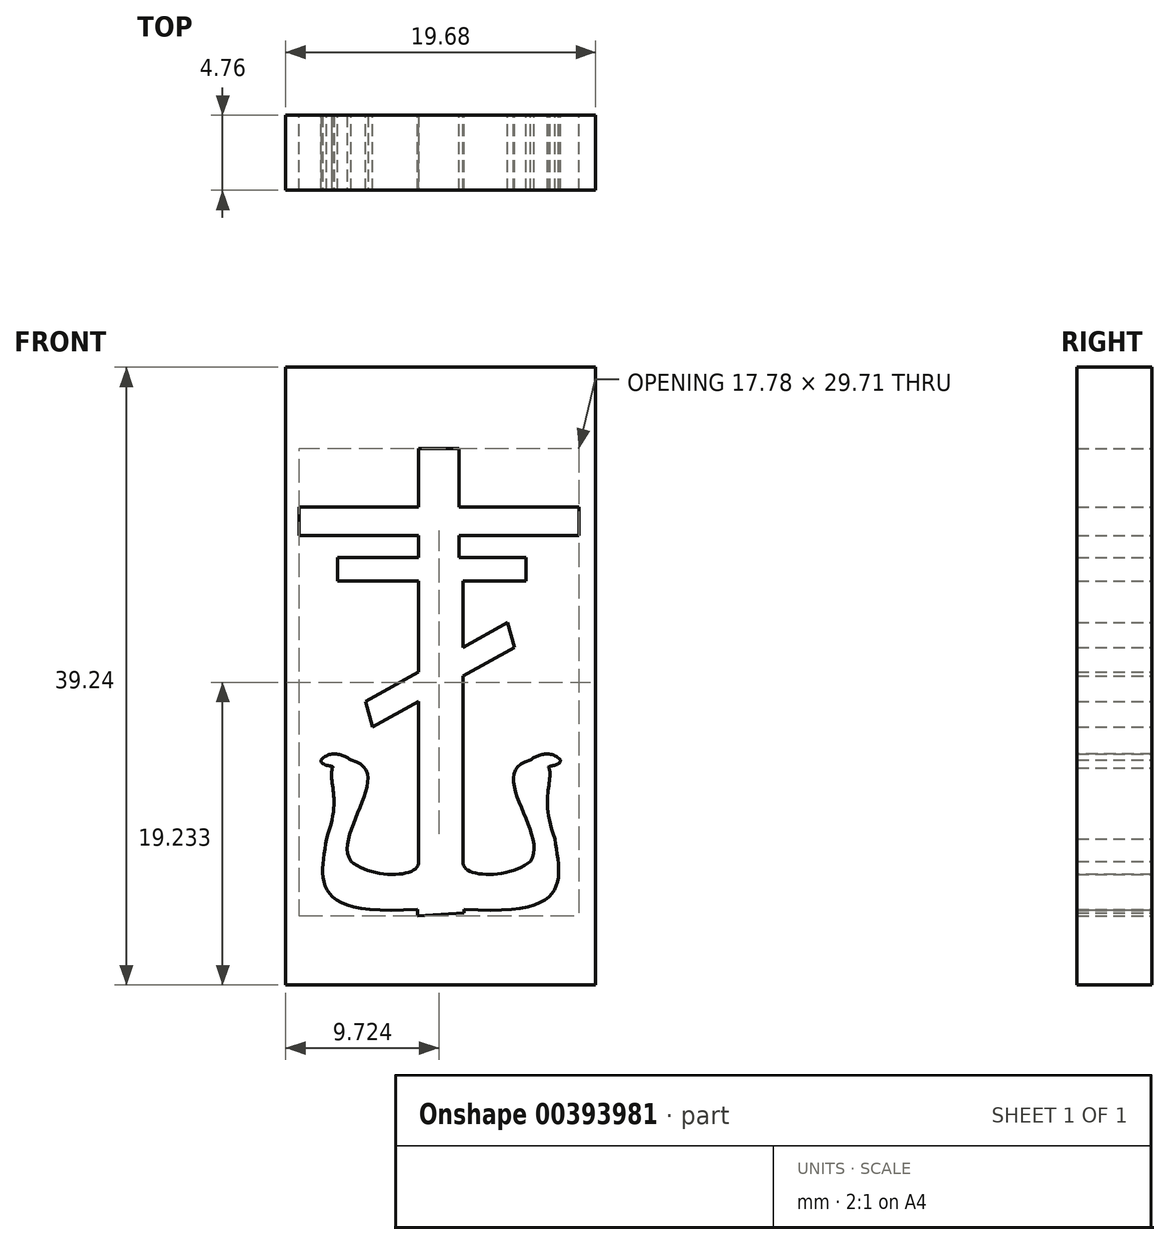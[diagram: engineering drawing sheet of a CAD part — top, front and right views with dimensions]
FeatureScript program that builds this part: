
annotation { "Feature Type Name" : "Feature", "Feature Type Description" : "" }
export const myFeature = defineFeature(function(context is Context, id is Id, definition is map)
    precondition{}
    {
        {
            var Q0;
            Q0=qCreatedBy(makeId("Front.planeOp"),FACE);
            var sketch = newSketch(context, id + "F0", { "sketchPlane" : qUnion([Q0])});
            skLineSegment(sketch, "E0", {"start": v(-1.42, 14.47) * mm, "end": v(1.15, 14.47) * mm});
            skLineSegment(sketch, "E1", {"start": v(1.15, 14.47) * mm, "end": v(1.15, 10.74) * mm});
            skLineSegment(sketch, "E2", {"start": v(1.15, 10.74) * mm, "end": v(8.77, 10.74) * mm});
            skLineSegment(sketch, "E3", {"start": v(8.77, 10.74) * mm, "end": v(8.77, 8.92) * mm});
            skLineSegment(sketch, "E4", {"start": v(8.77, 8.92) * mm, "end": v(1.15, 8.92) * mm});
            skLineSegment(sketch, "E5", {"start": v(1.15, 8.92) * mm, "end": v(1.15, 7.52) * mm});
            skLineSegment(sketch, "E6", {"start": v(1.15, 7.52) * mm, "end": v(5.42, 7.52) * mm});
            skLineSegment(sketch, "E7", {"start": v(5.42, 7.52) * mm, "end": v(5.42, 6.06) * mm});
            skLineSegment(sketch, "E8", {"start": v(5.42, 6.06) * mm, "end": v(1.42, 6.06) * mm});
            skLineSegment(sketch, "E9", {"start": v(1.42, 6.06) * mm, "end": v(1.42, 1.84) * mm});
            skLineSegment(sketch, "E10", {"start": v(1.42, 1.84) * mm, "end": v(4.24, 3.4) * mm});
            skLineSegment(sketch, "E11", {"start": v(4.68, 1.84) * mm, "end": v(4.24, 3.4) * mm});
            skLineSegment(sketch, "E12", {"start": v(4.68, 1.84) * mm, "end": v(1.42, 0) * mm});
            skLineSegment(sketch, "E13", {"start": v(1.42, 0) * mm, "end": v(1.42, -11.76) * mm});
            skLineSegment(sketch, "E14", {"start": v(-1.42, 14.47) * mm, "end": v(-1.42, 10.74) * mm});
            skLineSegment(sketch, "E15", {"start": v(-1.42, 10.74) * mm, "end": v(-9, 10.74) * mm});
            skLineSegment(sketch, "E16", {"start": v(-9, 10.74) * mm, "end": v(-9, 8.92) * mm});
            skLineSegment(sketch, "E17", {"start": v(-9, 8.92) * mm, "end": v(-1.42, 8.92) * mm});
            skLineSegment(sketch, "E18", {"start": v(-1.42, 8.92) * mm, "end": v(-1.42, 7.52) * mm});
            skLineSegment(sketch, "E19", {"start": v(-1.42, 7.52) * mm, "end": v(-6.54, 7.52) * mm});
            skLineSegment(sketch, "E20", {"start": v(-6.54, 7.52) * mm, "end": v(-6.54, 6.06) * mm});
            skLineSegment(sketch, "E21", {"start": v(-6.54, 6.06) * mm, "end": v(-1.42, 6.06) * mm});
            skLineSegment(sketch, "E22", {"start": v(-1.42, 6.06) * mm, "end": v(-1.42, 0.27) * mm});
            skLineSegment(sketch, "E23", {"start": v(-1.42, 0.27) * mm, "end": v(-4.78, -1.6) * mm});
            skLineSegment(sketch, "E24", {"start": v(-4.78, -1.6) * mm, "end": v(-4.31, -3.22) * mm});
            skLineSegment(sketch, "E25", {"start": v(-4.31, -3.22) * mm, "end": v(-1.42, -1.6) * mm});
            skLineSegment(sketch, "E26", {"start": v(-1.42, -1.6) * mm, "end": v(-1.42, -11.76) * mm});
            skFitSpline(sketch, "E27", {"points": [v(-1.42, -11.76) * mm, v(-5.7, -11.76) * mm], "startDerivative": vector(0.52, -3.23) * mm, "endDerivative": vector(-4, 3.45) * mm});
            skFitSpline(sketch, "E28", {"points": [v(-5.7, -11.76) * mm, v(-5.7, -5.32) * mm], "startDerivative": vector(-3.65, 5.14) * mm, "endDerivative": vector(-8.88, 2.16) * mm});
            skLineSegment(sketch, "E29", {"start": v(0, -19.76) * mm, "end": v(0, 16.73) * mm, "construction": true});
            skFitSpline(sketch, "E30.MirrorCS", {"points": [v(1.42, -11.76) * mm, v(5.7, -11.76) * mm], "startDerivative": vector(-0.52, -3.23) * mm, "endDerivative": vector(4, 3.45) * mm});
            skFitSpline(sketch, "E31.MirrorCS", {"points": [v(5.7, -11.76) * mm, v(5.7, -5.32) * mm], "startDerivative": vector(3.65, 5.14) * mm, "endDerivative": vector(8.88, 2.16) * mm});
            skFitSpline(sketch, "E32", {"points": [v(-5.7, -5.32) * mm, v(-7.6, -5.32) * mm], "startDerivative": vector(-1.08, 0.85) * mm, "endDerivative": vector(-1.8, -2.08) * mm});
            skFitSpline(sketch, "E33", {"points": [v(-7.6, -5.32) * mm, v(-6.89, -5.82) * mm], "startDerivative": vector(-0.1, -1.32) * mm, "endDerivative": vector(-0.78, -0.46) * mm});
            skFitSpline(sketch, "E34", {"points": [v(-6.89, -5.82) * mm, v(-7.26, -10.32) * mm], "startDerivative": vector(-0.73, -3.14) * mm, "endDerivative": vector(-2.94, -7.7) * mm});
            skFitSpline(sketch, "E35", {"points": [v(-7.26, -10.32) * mm, v(-1.48, -14.81) * mm], "startDerivative": vector(-0.93, -7.43) * mm, "endDerivative": vector(21.3, 1.5) * mm});
            skLineSegment(sketch, "E36", {"start": v(-1.48, -14.81) * mm, "end": v(-1.48, -15.24) * mm});
            skLineSegment(sketch, "E37", {"start": v(-1.48, -15.24) * mm, "end": v(1.5, -15.05) * mm});
            skLineSegment(sketch, "E38", {"start": v(1.5, -15.05) * mm, "end": v(1.48, -14.81) * mm});
            skFitSpline(sketch, "E39.MirrorCS", {"points": [v(5.7, -5.32) * mm, v(7.6, -5.32) * mm], "startDerivative": vector(1.08, 0.85) * mm, "endDerivative": vector(1.8, -2.08) * mm});
            skFitSpline(sketch, "E40.MirrorCS", {"points": [v(7.6, -5.32) * mm, v(6.89, -5.82) * mm], "startDerivative": vector(0.1, -1.32) * mm, "endDerivative": vector(0.78, -0.46) * mm});
            skFitSpline(sketch, "E41.MirrorCS", {"points": [v(6.89, -5.82) * mm, v(7.26, -10.32) * mm], "startDerivative": vector(0.73, -3.14) * mm, "endDerivative": vector(2.94, -7.7) * mm});
            skFitSpline(sketch, "E42.MirrorCS", {"points": [v(7.26, -10.32) * mm, v(1.48, -14.81) * mm], "startDerivative": vector(0.93, -7.43) * mm, "endDerivative": vector(-21.3, 1.5) * mm});
            skLineSegment(sketch, "E43.bottom", {"start": v(9.84, -19.62) * mm, "end": v(-9.84, -19.62) * mm});
            skLineSegment(sketch, "E43.top", {"start": v(9.84, 19.62) * mm, "end": v(-9.84, 19.62) * mm});
            skLineSegment(sketch, "E43.left", {"start": v(9.84, -19.62) * mm, "end": v(9.84, 19.62) * mm});
            skLineSegment(sketch, "E43.right", {"start": v(-9.84, -19.62) * mm, "end": v(-9.84, 19.62) * mm});
            skPoint(sketch, "E43.middle", {"position": v(0, 0) * mm});
            skSolve(sketch);
        }
        {
            var Q0;
            Q0=makeQuery(id+"F0.imprint","IMPRINT",FACE,{"disambiguationData":[TD([[makeQuery(id+"F0.imprint","IMPRINT",EDGE,{"derivedFrom":sQuery(id+"F0.wireOp",EDGE,"E0")}),1.0]])]});
            extrude(context, id + "F1", {"entities" : qUnion([Q0]), "depth" : 4.76 * mm});
        }
    });
